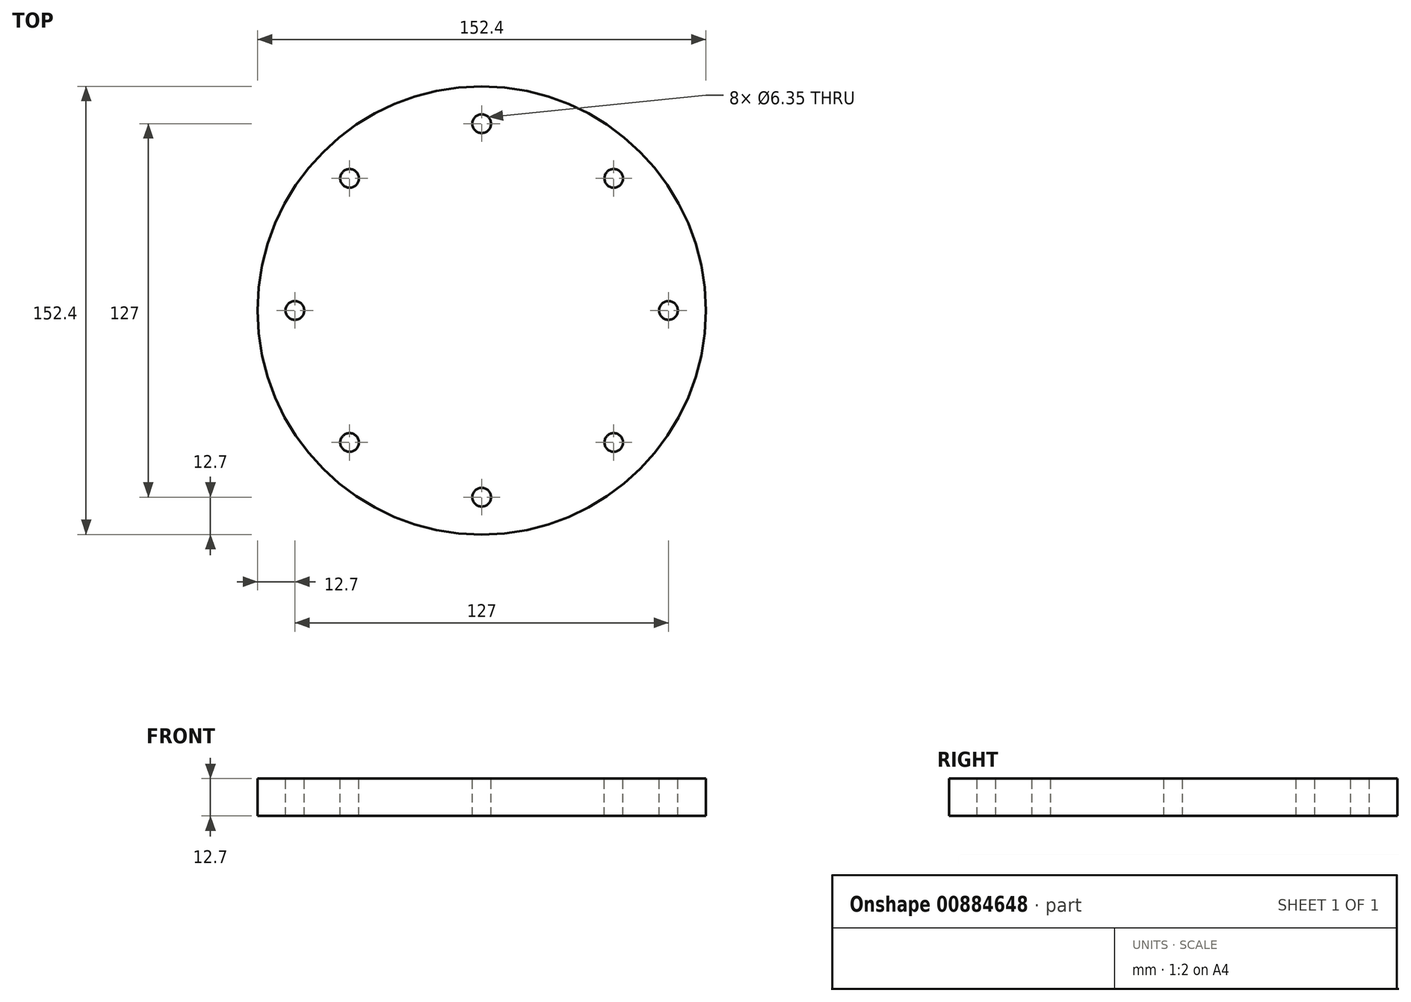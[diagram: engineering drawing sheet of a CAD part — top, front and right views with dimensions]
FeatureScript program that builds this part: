
annotation { "Feature Type Name" : "Feature", "Feature Type Description" : "" }
export const myFeature = defineFeature(function(context is Context, id is Id, definition is map)
    precondition{}
    {
        {
            var Q0;
            Q0=qCreatedBy(makeId("Top.planeOp"),FACE);
            var sketch = newSketch(context, id + "F0", { "sketchPlane" : qUnion([Q0])});
            skCircle(sketch, "E0", {"center": v(0, 0) * mm, "radius": 76.2 * mm});
            skSolve(sketch);
        }
        {
            var Q0;
            Q0=qCreatedBy(makeId("Top.planeOp"),FACE);
            var sketch = newSketch(context, id + "F1", { "sketchPlane" : qUnion([Q0])});
            skCircle(sketch, "E1", {"center": v(0, 63.5) * mm, "radius": 3.18 * mm});
            skCircle(sketch, "E2", {"center": v(63.5, 0) * mm, "radius": 3.17 * mm});
            skCircle(sketch, "E3", {"center": v(-63.5, 0) * mm, "radius": 3.18 * mm});
            skCircle(sketch, "E4", {"center": v(0, -63.5) * mm, "radius": 3.18 * mm});
            skCircle(sketch, "E5", {"center": v(-44.9, 44.9) * mm, "radius": 3.18 * mm});
            skCircle(sketch, "E6", {"center": v(44.9, 44.9) * mm, "radius": 3.17 * mm});
            skCircle(sketch, "E7", {"center": v(44.9, -44.9) * mm, "radius": 3.18 * mm});
            skCircle(sketch, "E8", {"center": v(-44.9, -44.9) * mm, "radius": 3.18 * mm});
            skSolve(sketch);
        }
        {
            var Q0;
            Q0 = qSketchRegion(id + "F0", true);
            extrude(context, id + "F2", {"entities" : qUnion([Q0]), "endBound" : BoundingType.SYMMETRIC, "depth" : 12.7 * mm, "offsetDistance" : 25.4 * mm});
        }
        {
            var Q0;
            Q0 = qSketchRegion(id + "F1", true);
            extrude(context, id + "F3", {"entities" : qUnion([Q0]), "operationType" : NewBodyOperationType.REMOVE, "endBound" : BoundingType.SYMMETRIC, "oppositeDirection" : true, "depth" : 12.7 * mm, "offsetDistance" : 25.4 * mm});
        }
    });
